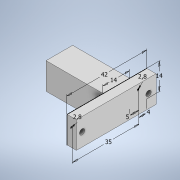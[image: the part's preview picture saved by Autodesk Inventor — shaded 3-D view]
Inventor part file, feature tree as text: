
AUTODESK INVENTOR PART (.ipt)
format: ipt  version: 2020.3 (Build 243373000, 373)  size: 253,440 bytes
history: native  units: mm
features: extrude x4, sketch x2
ambient origin geometry x8: Origin, YZ Plane, XZ Plane, XY Plane, X Axis, Y Axis, Z Axis, Center Point
bodies: Solid1 (feature_tree)
feature tree (6):
  sketch  "Sketch1"  dims[d0=5.0mm d1=0.0mm d2=30.0mm d3=0.0mm]
  extrude  "Extrusion1"  Depth=30.0mm TaperAngle=0.0deg
  extrude  "Extrusion2"  Depth=42.0mm
  extrude  "Extrusion5"  Depth=14.0mm
  extrude  "Extrusion6"  Depth=10.0mm
  sketch  "Sketch4"  dims[d10=14.0mm d11=42.0mm d12=14.0mm d14=2.8mm d15=2.8mm d16=35.0mm d17=4.0mm d18=5.0mm d19=2.8mm d20=10.0mm d21=0.0mm d22=10.0mm d23=0.0mm]
